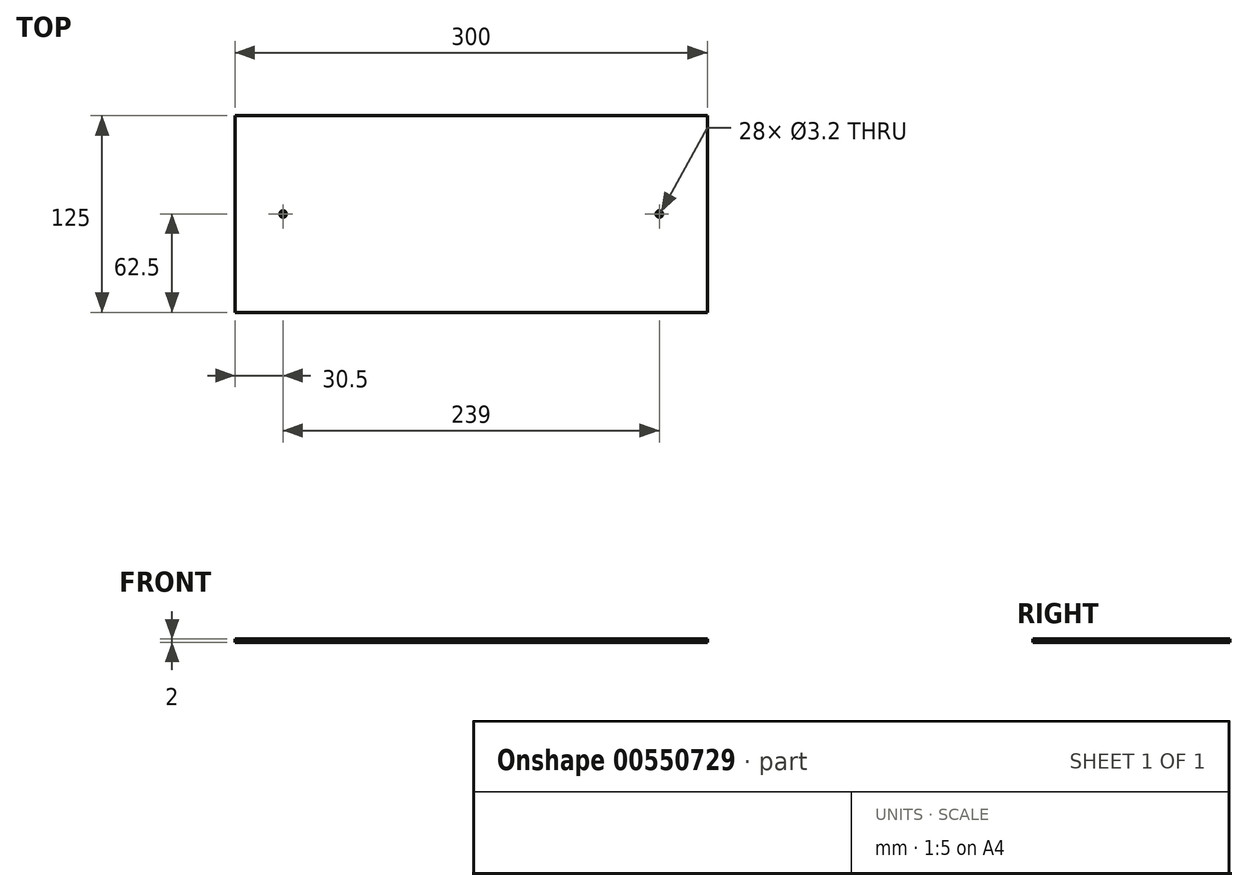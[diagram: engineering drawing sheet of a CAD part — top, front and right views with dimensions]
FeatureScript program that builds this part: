
annotation { "Feature Type Name" : "Feature", "Feature Type Description" : "" }
export const myFeature = defineFeature(function(context is Context, id is Id, definition is map)
    precondition{}
    {
        {
            var Q0;
            Q0=qCreatedBy(makeId("Top.planeOp"),FACE);
            var sketch = newSketch(context, id + "F0", { "sketchPlane" : qUnion([Q0])});
            skLineSegment(sketch, "E0.rect.bottom", {"start": v(-150, 62.5) * mm, "end": v(150, 62.5) * mm});
            skLineSegment(sketch, "E0.rect.top", {"start": v(-150, -62.5) * mm, "end": v(150, -62.5) * mm});
            skLineSegment(sketch, "E0.rect.left", {"start": v(-150, 62.5) * mm, "end": v(-150, -62.5) * mm});
            skLineSegment(sketch, "E0.rect.right", {"start": v(150, 62.5) * mm, "end": v(150, -62.5) * mm});
            skPoint(sketch, "E0.rect.middle", {"position": v(0, 0) * mm});
            skCircle(sketch, "E1", {"center": v(-119.5, 0) * mm, "radius": 1.6 * mm});
            skLineSegment(sketch, "E2", {"start": v(0, 62.5) * mm, "end": v(0, -62.5) * mm, "construction": true});
            skCircle(sketch, "E3.0.MirrorC", {"center": v(119.5, 0) * mm, "radius": 1.6 * mm});
            skSolve(sketch);
        }
        {
            var Q0;
            Q0=qSketchRegion(id+"F0",true);
            extrude(context, id + "F1", {"entities" : qUnion([Q0]), "depth" : 2 * mm});
        }
        {
            var Q0;
            Q0=makeQuery(id+"F1.opExtrude","SWEPT_FACE",FACE,{"disambiguationData":[OSD([sQuery(id+"F0.wireOp",EDGE,"E1")])]});
            var Q1;
            Q1=makeQuery(id+"F1.opExtrude","SWEPT_FACE",FACE,{"disambiguationData":[OSD([sQuery(id+"F0.wireOp",EDGE,"E3.0.MirrorC")])]});
            chamfer(context, id + "F2", {"entities" : qUnion([Q0, Q1]), "width" : 0.5 * mm, "tangentPropagation" : true});
        }
    });
